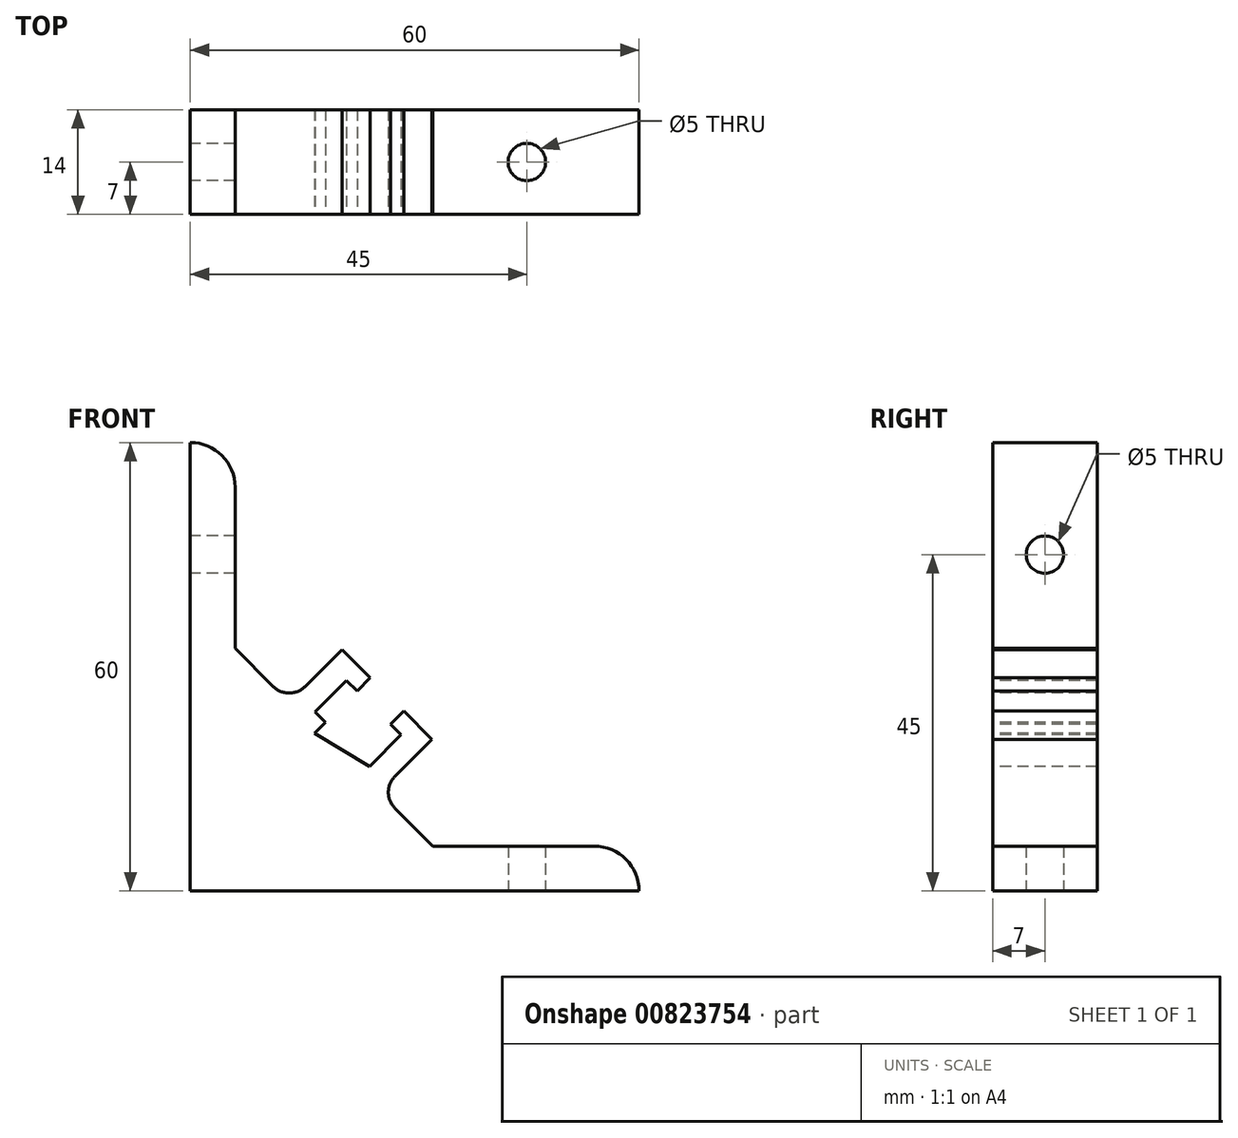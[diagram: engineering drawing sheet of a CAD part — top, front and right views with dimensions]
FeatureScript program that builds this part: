
annotation { "Feature Type Name" : "Feature", "Feature Type Description" : "" }
export const myFeature = defineFeature(function(context is Context, id is Id, definition is map)
    precondition{}
    {
        {
            var Q0;
            Q0=qCreatedBy(makeId("Front.planeOp"),FACE);
            var sketch = newSketch(context, id + "F0", { "sketchPlane" : qUnion([Q0])});
            skLineSegment(sketch, "E0", {"start": v(0, 60) * mm, "end": v(0, 0) * mm});
            skLineSegment(sketch, "E1", {"start": v(0, 0) * mm, "end": v(60, 0) * mm});
            skArc(sketch, "E2", {"start": v(4, 4.5) * mm, "mid": v(4.15, 4.15) * mm, "end": v(4.5, 4) * mm});
            skLineSegment(sketch, "E3", {"start": v(4.5, 4) * mm, "end": v(29, 4) * mm});
            skArc(sketch, "E4", {"start": v(29, 4) * mm, "mid": v(29.46, 4.3) * mm, "end": v(29.35, 4.85) * mm});
            skLineSegment(sketch, "E5", {"start": v(4, 29) * mm, "end": v(4, 4.5) * mm});
            skArc(sketch, "E6", {"start": v(4.85, 29.35) * mm, "mid": v(4.3, 29.46) * mm, "end": v(4, 29) * mm});
            skLineSegment(sketch, "E7", {"start": v(4.85, 29.35) * mm, "end": v(13.57, 20.64) * mm});
            skLineSegment(sketch, "E8", {"start": v(20.64, 13.57) * mm, "end": v(29.35, 4.85) * mm});
            skLineSegment(sketch, "E9", {"start": v(54, 6) * mm, "end": v(32.45, 6) * mm});
            skArc(sketch, "E10", {"start": v(60, 0) * mm, "mid": v(58.24, 4.24) * mm, "end": v(54, 6) * mm});
            skLineSegment(sketch, "E11", {"start": v(6, 54) * mm, "end": v(6, 32.45) * mm});
            skArc(sketch, "E12", {"start": v(6, 54) * mm, "mid": v(4.24, 58.24) * mm, "end": v(0, 60) * mm});
            skLineSegment(sketch, "E13", {"start": v(27.36, 11.1) * mm, "end": v(32.45, 6) * mm});
            skArc(sketch, "E14", {"start": v(27.36, 15.34) * mm, "mid": v(26.48, 13.21) * mm, "end": v(27.36, 11.1) * mm});
            skLineSegment(sketch, "E15", {"start": v(6, 32.45) * mm, "end": v(11.1, 27.36) * mm});
            skArc(sketch, "E16", {"start": v(11.1, 27.36) * mm, "mid": v(13.21, 26.48) * mm, "end": v(15.34, 27.36) * mm});
            skLineSegment(sketch, "E17", {"start": v(24.07, 28.52) * mm, "end": v(20.29, 32.3) * mm});
            skLineSegment(sketch, "E18", {"start": v(15.34, 27.36) * mm, "end": v(20.29, 32.3) * mm});
            skLineSegment(sketch, "E19", {"start": v(28.52, 24.07) * mm, "end": v(32.3, 20.29) * mm});
            skLineSegment(sketch, "E20", {"start": v(27.36, 15.34) * mm, "end": v(32.3, 20.29) * mm});
            skLineSegment(sketch, "E21", {"start": v(28.52, 24.07) * mm, "end": v(26.76, 22.3) * mm});
            skLineSegment(sketch, "E22", {"start": v(28.17, 20.89) * mm, "end": v(23.96, 16.68) * mm});
            skLineSegment(sketch, "E23", {"start": v(26.76, 22.3) * mm, "end": v(28.17, 20.89) * mm});
            skLineSegment(sketch, "E24", {"start": v(24.07, 28.52) * mm, "end": v(22.3, 26.76) * mm});
            skLineSegment(sketch, "E25", {"start": v(22.3, 26.76) * mm, "end": v(20.89, 28.17) * mm});
            skLineSegment(sketch, "E26", {"start": v(20.89, 28.17) * mm, "end": v(16.68, 23.96) * mm});
            skLineSegment(sketch, "E27", {"start": v(16.64, 21.1) * mm, "end": v(18.1, 22.55) * mm});
            skLineSegment(sketch, "E28", {"start": v(16.68, 23.96) * mm, "end": v(18.1, 22.55) * mm});
            skLineSegment(sketch, "E29", {"start": v(16.64, 21.1) * mm, "end": v(23.96, 16.68) * mm});
            skLineSegment(sketch, "E30", {"start": v(45, -1.83) * mm, "end": v(45, 8.9) * mm});
            skLineSegment(sketch, "E31", {"start": v(-1.23, 45) * mm, "end": v(8.9, 45) * mm});
            skArc(sketch, "E32", {"start": v(15.83, 9.9) * mm, "mid": v(17.17, 10.39) * mm, "end": v(18.31, 11.24) * mm});
            skArc(sketch, "E33", {"start": v(11.24, 18.32) * mm, "mid": v(10.39, 17.17) * mm, "end": v(9.9, 15.83) * mm});
            skLineSegment(sketch, "E34", {"start": v(12.36, 14.13) * mm, "end": v(11.75, 13.97) * mm});
            skLineSegment(sketch, "E35", {"start": v(14.13, 12.36) * mm, "end": v(13.97, 11.75) * mm});
            skArc(sketch, "E36", {"start": v(14.13, 12.36) * mm, "mid": v(16.55, 16.55) * mm, "end": v(12.36, 14.13) * mm});
            skLineSegment(sketch, "E37", {"start": v(15.83, 9.9) * mm, "end": v(13.97, 11.75) * mm});
            skLineSegment(sketch, "E38", {"start": v(20.64, 13.57) * mm, "end": v(18.31, 11.24) * mm});
            skLineSegment(sketch, "E39", {"start": v(9.9, 15.83) * mm, "end": v(11.75, 13.97) * mm});
            skLineSegment(sketch, "E40", {"start": v(13.57, 20.64) * mm, "end": v(11.24, 18.32) * mm});
            skSolve(sketch);
        }
        {
            var Q0;
            {var subQ0=sQuery(id+"F0.wireOp",EDGE,"E12");Q0=makeQuery(id+"F0.imprint","IMPRINT",FACE,{"disambiguationData":[TD([[makeQuery(id+"F0.imprint","IMPRINT",EDGE,{"derivedFrom":subQ0}),1.0]])]});}
            var Q1;
            {var subQ0=sQuery(id+"F0.wireOp",EDGE,"E10");Q1=makeQuery(id+"F0.imprint","IMPRINT",FACE,{"disambiguationData":[TD([[makeQuery(id+"F0.imprint","IMPRINT",EDGE,{"derivedFrom":subQ0}),1.0]])]});}
            var Q2;
            Q2=makeQuery(id+"F0.imprint","IMPRINT",FACE,{"disambiguationData":[TD([[makeQuery(id+"F0.imprint","IMPRINT",EDGE,{"derivedFrom":sQuery(id+"F0.wireOp",EDGE,"E2")}),1.0]])]});
            var Q3;
            Q3=makeQuery(id+"F0.imprint","IMPRINT",FACE,{"disambiguationData":[TD([[makeQuery(id+"F0.imprint","IMPRINT",EDGE,{"derivedFrom":sQuery(id+"F0.wireOp",EDGE,"E2")}),-1.0]])]});
            extrude(context, id + "F1", {"entities" : qUnion([Q0, Q1, Q2, Q3]), "oppositeDirection" : true, "depth" : 14 * mm, "offsetDistance" : 25 * mm});
        }
        {
            var Q0;
            Q0=makeQuery(id+"F1.opExtrude","SWEPT_FACE",FACE,{"disambiguationData":[OSD([sQuery(id+"F0.wireOp",EDGE,"E0")])]});
            var sketch = newSketch(context, id + "F2", { "sketchPlane" : qUnion([Q0])});
            skCircle(sketch, "E41", {"center": v(-7, 45) * mm, "radius": 2.5 * mm});
            skSolve(sketch);
        }
        {
            var Q0;
            Q0 = qSketchRegion(id + "F2", true);
            extrude(context, id + "F3", {"entities" : qUnion([Q0]), "operationType" : NewBodyOperationType.REMOVE, "oppositeDirection" : true, "depth" : 6 * mm, "offsetDistance" : 25 * mm});
        }
        {
            var Q0;
            Q0=makeQuery(id+"F1.opExtrude","SWEPT_FACE",FACE,{"disambiguationData":[OSD([sQuery(id+"F0.wireOp",EDGE,"E1")])]});
            var sketch = newSketch(context, id + "F4", { "sketchPlane" : qUnion([Q0])});
            skLineSegment(sketch, "E42", {"start": v(39.31, 0) * mm, "end": v(71.4, 0) * mm});
            skCircle(sketch, "E43", {"center": v(45, -7) * mm, "radius": 2.5 * mm});
            skSolve(sketch);
        }
        {
            var Q0;
            Q0 = qSketchRegion(id + "F4", true);
            extrude(context, id + "F5", {"entities" : qUnion([Q0]), "operationType" : NewBodyOperationType.REMOVE, "oppositeDirection" : true, "depth" : 6 * mm, "offsetDistance" : 25 * mm});
        }
    });
